# Revit family: PRD_FrankeWS_SlbUrnls_SiphonCoverplateForTroughUrinal_ZCMPX0010
name_source: partatom
category: Furniture
revit_build: Autodesk Revit 2018 (Build: 20190510_1515(x64)
units: mm (PartAtom-declared; Revit-internal decimal feet)

## family parameters
Cut with Voids When Loaded = No
Host = Face
OmniClass Number = 23.40.20.00
OmniClass Title = General Furniture and Specialties
Room Calculation Point = No
Shared = No

## types (1)
- ZCMPX0010
    AssetType = Fixed
    BIMObjectName = PRD_AR_SlabUrinals_SiphonCoverplateForTroughUrinal_ZCMPX0010
    Category = Pr_40_20_93_77, Slab urinals
    Color = Stainless steel
    CoverplateMaterial = PRD_AR_StainlessSteel_SatinFinished
    Default Elevation = 535 mm  [stored 1.75525 ft]
    Description = Siphon coverplate for trough urinal CMPX551 - CMPX555, stainless steel, surface satin finished, material thickness 1,5 mm. To cover the Siphon under the trough urinal.
    DurationUnit = year
    Features = stainless steel, surface satin finished, material thickness 1,5 mm
    Finish = Satin finished
    IfcExportAs = IfcBuildingElementProxy
    IfcExportType = NOTDEFINED
    Manufacturer = KWC Group AG
    ManufacturerName = KWC Group AG
    ManufacturerURL = www.kwc.com
    Material = Stainless steel
    Model = ZCMPX0010
    ModelNumber = 2000102739
    ModelReference = ZCMPX0010
    NBSDescription = Urinal assembly
    NBSReference = 45-35-70/352
    Name = Siphon coverplate for trough urinal ZCMPX0010
    NominalHeight = 365 mm  [stored 1.19751 ft]
    NominalLength = 340 mm  [stored 1.11549 ft]
    NominalWidth = 150 mm
    ProductInformation = https://pim.kwc.com
    URL = www.kwc.com
    Uniclass2015Code = Pr_40_20_93_77
    Uniclass2015Title = Slab urinals
    Uniclass2015Version = Products v1.5
    Version = 1
    WarrantyDurationUnit = year

note: [stored X ft] marks values corroborated as IEEE doubles in the binary element streams (Revit-internal decimal feet)

## geometry (parser evidence)
native form markers: Sweep x3
no freeform markers — native parametric forms only
